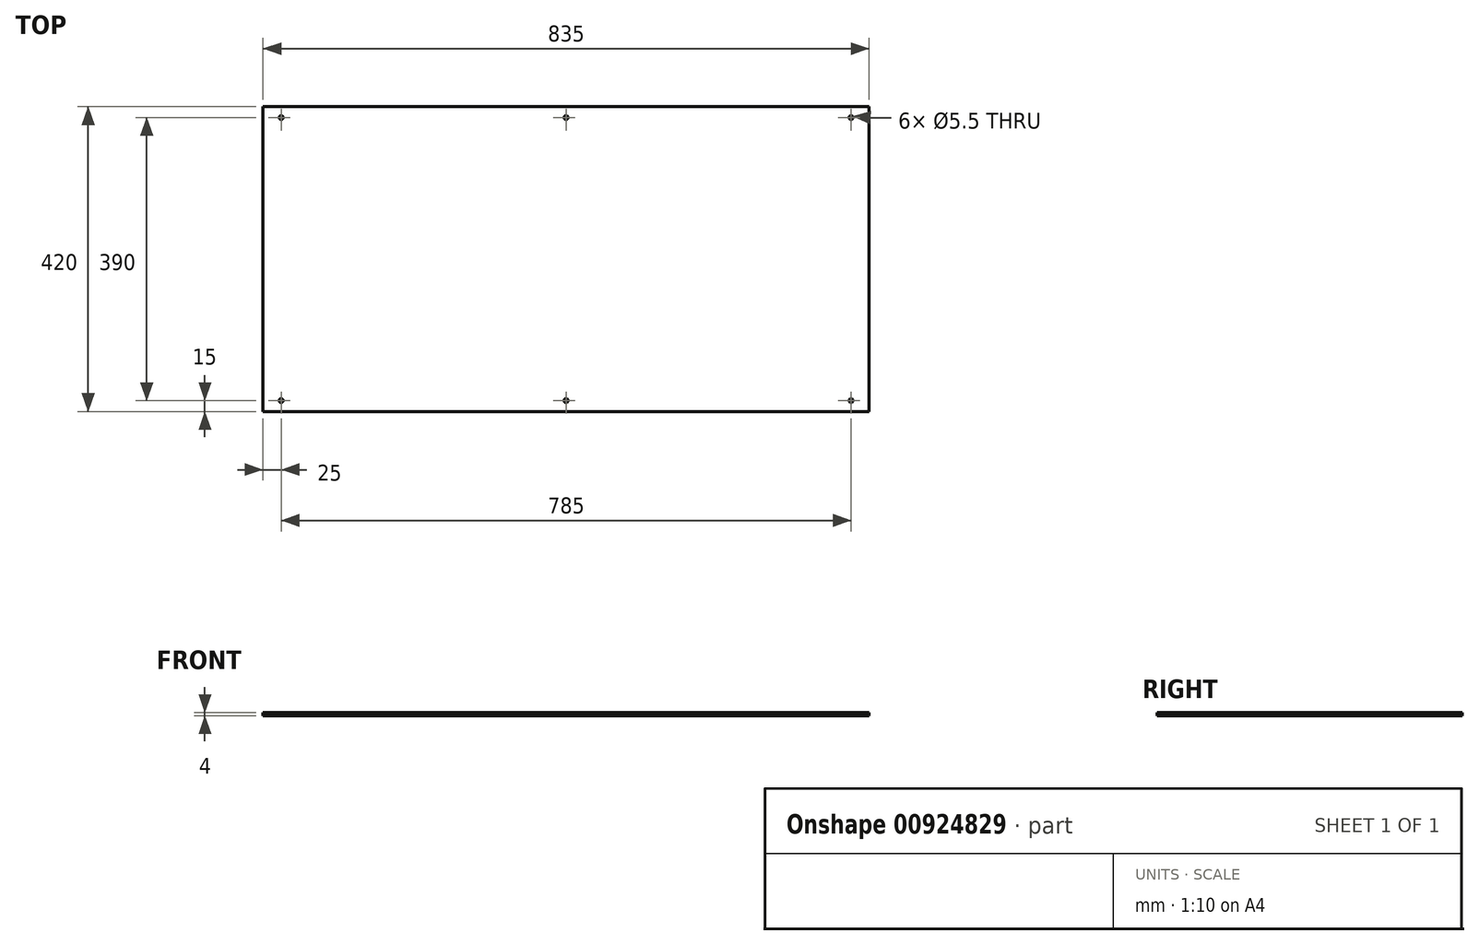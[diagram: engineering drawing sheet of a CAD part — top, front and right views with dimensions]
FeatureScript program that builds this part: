
annotation { "Feature Type Name" : "Feature", "Feature Type Description" : "" }
export const myFeature = defineFeature(function(context is Context, id is Id, definition is map)
    precondition{}
    {
        {
            var Q0;
            Q0=qCreatedBy(makeId("Top.planeOp"),FACE);
            var sketch = newSketch(context, id + "F0", { "sketchPlane" : qUnion([Q0])});
            skLineSegment(sketch, "E0.bottom", {"start": v(417.5, -210) * mm, "end": v(-417.5, -210) * mm});
            skLineSegment(sketch, "E0.top", {"start": v(417.5, 210) * mm, "end": v(-417.5, 210) * mm});
            skLineSegment(sketch, "E0.left", {"start": v(417.5, -210) * mm, "end": v(417.5, 210) * mm});
            skLineSegment(sketch, "E0.right", {"start": v(-417.5, -210) * mm, "end": v(-417.5, 210) * mm});
            skPoint(sketch, "E0.middle", {"position": v(0, 0) * mm});
            skCircle(sketch, "E1", {"center": v(-392.5, 195) * mm, "radius": 2.75 * mm});
            skCircle(sketch, "E2", {"center": v(0, 195) * mm, "radius": 2.75 * mm});
            skCircle(sketch, "E3", {"center": v(392.5, 195) * mm, "radius": 2.75 * mm});
            skCircle(sketch, "E4.MirrorC", {"center": v(-392.5, -195) * mm, "radius": 2.75 * mm});
            skCircle(sketch, "E5.MirrorC", {"center": v(0, -195) * mm, "radius": 2.75 * mm});
            skCircle(sketch, "E6.MirrorC", {"center": v(392.5, -195) * mm, "radius": 2.75 * mm});
            skSolve(sketch);
        }
        {
            var Q0;
            Q0 = qSketchRegion(id + "F0", true);
            extrude(context, id + "F1", {"entities" : qUnion([Q0]), "depth" : 4 * mm, "offsetDistance" : 25 * mm});
        }
    });
